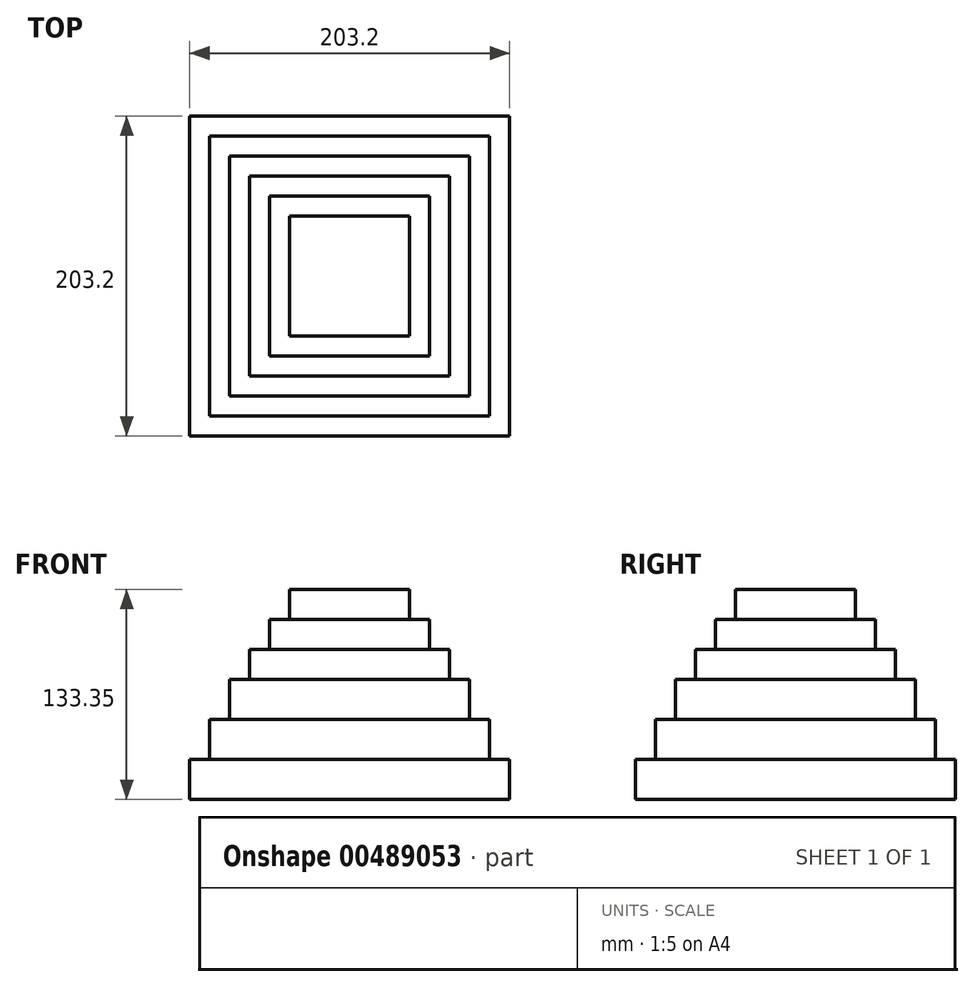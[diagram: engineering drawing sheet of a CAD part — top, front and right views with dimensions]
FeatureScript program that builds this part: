
annotation { "Feature Type Name" : "Feature", "Feature Type Description" : "" }
export const myFeature = defineFeature(function(context is Context, id is Id, definition is map)
    precondition{}
    {
        {
            var Q0;
            Q0=qCreatedBy(makeId("Top.planeOp"),FACE);
            var sketch = newSketch(context, id + "F0", { "sketchPlane" : qUnion([Q0])});
            skLineSegment(sketch, "E0.bottom", {"start": v(0, 0) * mm, "end": v(101.6, 0) * mm});
            skLineSegment(sketch, "E0.top", {"start": v(0, 101.6) * mm, "end": v(101.6, 101.6) * mm});
            skLineSegment(sketch, "E0.left", {"start": v(0, 0) * mm, "end": v(0, 101.6) * mm});
            skLineSegment(sketch, "E0.right", {"start": v(101.6, 0) * mm, "end": v(101.6, 101.6) * mm});
            skLineSegment(sketch, "E1.bottom", {"start": v(0, 0) * mm, "end": v(-101.6, 0) * mm});
            skLineSegment(sketch, "E1.top", {"start": v(0, -101.6) * mm, "end": v(-101.6, -101.6) * mm});
            skLineSegment(sketch, "E1.left", {"start": v(0, 0) * mm, "end": v(0, -101.6) * mm});
            skLineSegment(sketch, "E1.right", {"start": v(-101.6, 0) * mm, "end": v(-101.6, -101.6) * mm});
            skLineSegment(sketch, "E2.top", {"start": v(0, -101.6) * mm, "end": v(101.6, -101.6) * mm});
            skLineSegment(sketch, "E2.right", {"start": v(101.6, 0) * mm, "end": v(101.6, -101.6) * mm});
            skLineSegment(sketch, "E3.top", {"start": v(0, 101.6) * mm, "end": v(-101.6, 101.6) * mm});
            skLineSegment(sketch, "E3.right", {"start": v(-101.6, 0) * mm, "end": v(-101.6, 101.6) * mm});
            skSolve(sketch);
        }
        {
            var Q0;
            Q0 = qSketchRegion(id + "F0", true);
            extrude(context, id + "F1", {"entities" : qUnion([Q0]), "depth" : 25.4 * mm});
        }
        {
            var Q0;
            Q0=makeQuery(id+"F1.opExtrude","CAP_FACE",FACE,{"disambiguationData":[OSD([sQuery(id+"F0.wireOp",EDGE,"E0.top"),sQuery(id+"F0.wireOp",EDGE,"E0.right"),sQuery(id+"F0.wireOp",EDGE,"E1.top"),sQuery(id+"F0.wireOp",EDGE,"E1.right"),sQuery(id+"F0.wireOp",EDGE,"E2.top"),sQuery(id+"F0.wireOp",EDGE,"E2.right"),sQuery(id+"F0.wireOp",EDGE,"E3.top"),sQuery(id+"F0.wireOp",EDGE,"E3.right")])],"isStart":false});
            var sketch = newSketch(context, id + "F2", { "sketchPlane" : qUnion([Q0])});
            skLineSegment(sketch, "E4.bottom", {"start": v(0, 0) * mm, "end": v(-88.9, 0) * mm});
            skLineSegment(sketch, "E4.top", {"start": v(0, 88.9) * mm, "end": v(-88.9, 88.9) * mm});
            skLineSegment(sketch, "E4.left", {"start": v(0, 0) * mm, "end": v(0, 88.9) * mm});
            skLineSegment(sketch, "E4.right", {"start": v(-88.9, 0) * mm, "end": v(-88.9, 88.9) * mm});
            skLineSegment(sketch, "E5.bottom", {"start": v(0, 0) * mm, "end": v(88.9, 0) * mm});
            skLineSegment(sketch, "E5.top", {"start": v(0, 88.9) * mm, "end": v(88.9, 88.9) * mm});
            skLineSegment(sketch, "E5.right", {"start": v(88.9, 0) * mm, "end": v(88.9, 88.9) * mm});
            skLineSegment(sketch, "E6.top", {"start": v(0, -88.9) * mm, "end": v(88.9, -88.9) * mm});
            skLineSegment(sketch, "E6.left", {"start": v(0, 0) * mm, "end": v(0, -88.9) * mm});
            skLineSegment(sketch, "E6.right", {"start": v(88.9, 0) * mm, "end": v(88.9, -88.9) * mm});
            skLineSegment(sketch, "E7.top", {"start": v(0, -88.9) * mm, "end": v(-88.9, -88.9) * mm});
            skLineSegment(sketch, "E7.right", {"start": v(-88.9, 0) * mm, "end": v(-88.9, -88.9) * mm});
            skSolve(sketch);
        }
        {
            var Q0;
            Q0=makeQuery(id+"F2.imprint","IMPRINT",FACE,{"disambiguationData":[TD([[makeQuery(id+"F2.imprint","IMPRINT",EDGE,{"derivedFrom":sQuery(id+"F2.wireOp",EDGE,"E5.top")}),-1.0]])]});
            var Q1;
            Q1=makeQuery(id+"F2.imprint","IMPRINT",FACE,{"disambiguationData":[TD([[makeQuery(id+"F2.imprint","IMPRINT",EDGE,{"derivedFrom":sQuery(id+"F2.wireOp",EDGE,"E5.bottom")}),-1.0]])]});
            var Q2;
            Q2=makeQuery(id+"F2.imprint","IMPRINT",FACE,{"disambiguationData":[TD([[makeQuery(id+"F2.imprint","IMPRINT",EDGE,{"derivedFrom":sQuery(id+"F2.wireOp",EDGE,"E4.bottom")}),1.0]])]});
            var Q3;
            Q3=makeQuery(id+"F2.imprint","IMPRINT",FACE,{"disambiguationData":[TD([[makeQuery(id+"F2.imprint","IMPRINT",EDGE,{"derivedFrom":sQuery(id+"F2.wireOp",EDGE,"E4.top")}),1.0]])]});
            extrude(context, id + "F3", {"entities" : qUnion([Q0, Q1, Q2, Q3]), "operationType" : NewBodyOperationType.ADD, "depth" : 25.4 * mm});
        }
        {
            var Q0;
            Q0=makeQuery(id+"F3.opExtrude","CAP_FACE",FACE,{"disambiguationData":[OSD([sQuery(id+"F2.wireOp",EDGE,"E4.top"),sQuery(id+"F2.wireOp",EDGE,"E4.right"),sQuery(id+"F2.wireOp",EDGE,"E5.top"),sQuery(id+"F2.wireOp",EDGE,"E5.right"),sQuery(id+"F2.wireOp",EDGE,"E6.top"),sQuery(id+"F2.wireOp",EDGE,"E6.right"),sQuery(id+"F2.wireOp",EDGE,"E7.top"),sQuery(id+"F2.wireOp",EDGE,"E7.right")])],"isStart":false});
            var sketch = newSketch(context, id + "F4", { "sketchPlane" : qUnion([Q0])});
            skLineSegment(sketch, "E8.bottom", {"start": v(0, 0) * mm, "end": v(-76.2, 0) * mm});
            skLineSegment(sketch, "E8.top", {"start": v(0, 76.2) * mm, "end": v(-76.2, 76.2) * mm});
            skLineSegment(sketch, "E8.left", {"start": v(0, 0) * mm, "end": v(0, 76.2) * mm});
            skLineSegment(sketch, "E8.right", {"start": v(-76.2, 0) * mm, "end": v(-76.2, 76.2) * mm});
            skLineSegment(sketch, "E9.bottom", {"start": v(0, 0) * mm, "end": v(76.2, 0) * mm});
            skLineSegment(sketch, "E9.top", {"start": v(0, 76.2) * mm, "end": v(76.2, 76.2) * mm});
            skLineSegment(sketch, "E9.right", {"start": v(76.2, 0) * mm, "end": v(76.2, 76.2) * mm});
            skLineSegment(sketch, "E10.top", {"start": v(0, -76.2) * mm, "end": v(76.2, -76.2) * mm});
            skLineSegment(sketch, "E10.left", {"start": v(0, 0) * mm, "end": v(0, -76.2) * mm});
            skLineSegment(sketch, "E10.right", {"start": v(76.2, 0) * mm, "end": v(76.2, -76.2) * mm});
            skLineSegment(sketch, "E11.top", {"start": v(0, -76.2) * mm, "end": v(-76.2, -76.2) * mm});
            skLineSegment(sketch, "E11.right", {"start": v(-76.2, 0) * mm, "end": v(-76.2, -76.2) * mm});
            skSolve(sketch);
        }
        {
            var Q0;
            Q0=makeQuery(id+"F4.imprint","IMPRINT",FACE,{"disambiguationData":[TD([[makeQuery(id+"F4.imprint","IMPRINT",EDGE,{"derivedFrom":sQuery(id+"F4.wireOp",EDGE,"E9.top")}),-1.0]])]});
            var Q1;
            Q1=makeQuery(id+"F4.imprint","IMPRINT",FACE,{"disambiguationData":[TD([[makeQuery(id+"F4.imprint","IMPRINT",EDGE,{"derivedFrom":sQuery(id+"F4.wireOp",EDGE,"E9.bottom")}),-1.0]])]});
            var Q2;
            Q2=makeQuery(id+"F4.imprint","IMPRINT",FACE,{"disambiguationData":[TD([[makeQuery(id+"F4.imprint","IMPRINT",EDGE,{"derivedFrom":sQuery(id+"F4.wireOp",EDGE,"E8.bottom")}),1.0]])]});
            var Q3;
            Q3=makeQuery(id+"F4.imprint","IMPRINT",FACE,{"disambiguationData":[TD([[makeQuery(id+"F4.imprint","IMPRINT",EDGE,{"derivedFrom":sQuery(id+"F4.wireOp",EDGE,"E8.top")}),1.0]])]});
            extrude(context, id + "F5", {"entities" : qUnion([Q0, Q1, Q2, Q3]), "operationType" : NewBodyOperationType.ADD, "depth" : 25.4 * mm});
        }
        {
            var Q0;
            Q0=makeQuery(id+"F5.opExtrude","CAP_FACE",FACE,{"disambiguationData":[OSD([sQuery(id+"F4.wireOp",EDGE,"E8.top"),sQuery(id+"F4.wireOp",EDGE,"E8.right"),sQuery(id+"F4.wireOp",EDGE,"E9.top"),sQuery(id+"F4.wireOp",EDGE,"E9.right"),sQuery(id+"F4.wireOp",EDGE,"E10.top"),sQuery(id+"F4.wireOp",EDGE,"E10.right"),sQuery(id+"F4.wireOp",EDGE,"E11.top"),sQuery(id+"F4.wireOp",EDGE,"E11.right")])],"isStart":false});
            var sketch = newSketch(context, id + "F6", { "sketchPlane" : qUnion([Q0])});
            skLineSegment(sketch, "E12.bottom", {"start": v(0, 0) * mm, "end": v(-63.5, 0) * mm});
            skLineSegment(sketch, "E12.top", {"start": v(0, 63.5) * mm, "end": v(-63.5, 63.5) * mm});
            skLineSegment(sketch, "E12.left", {"start": v(0, 0) * mm, "end": v(0, 63.5) * mm});
            skLineSegment(sketch, "E12.right", {"start": v(-63.5, 0) * mm, "end": v(-63.5, 63.5) * mm});
            skLineSegment(sketch, "E13.bottom", {"start": v(0, 0) * mm, "end": v(63.5, 0) * mm});
            skLineSegment(sketch, "E13.top", {"start": v(0, -63.5) * mm, "end": v(63.5, -63.5) * mm});
            skLineSegment(sketch, "E13.left", {"start": v(0, 0) * mm, "end": v(0, -63.5) * mm});
            skLineSegment(sketch, "E13.right", {"start": v(63.5, 0) * mm, "end": v(63.5, -63.5) * mm});
            skLineSegment(sketch, "E14.top", {"start": v(0, -63.5) * mm, "end": v(-63.5, -63.5) * mm});
            skLineSegment(sketch, "E14.right", {"start": v(-63.5, 0) * mm, "end": v(-63.5, -63.5) * mm});
            skLineSegment(sketch, "E15.top", {"start": v(0, 63.5) * mm, "end": v(63.5, 63.5) * mm});
            skLineSegment(sketch, "E15.right", {"start": v(63.5, 0) * mm, "end": v(63.5, 63.5) * mm});
            skSolve(sketch);
        }
        {
            var Q0;
            Q0=makeQuery(id+"F6.imprint","IMPRINT",FACE,{"disambiguationData":[TD([[makeQuery(id+"F6.imprint","IMPRINT",EDGE,{"derivedFrom":sQuery(id+"F6.wireOp",EDGE,"E13.top")}),1.0]])]});
            var Q1;
            Q1=makeQuery(id+"F6.imprint","IMPRINT",FACE,{"disambiguationData":[TD([[makeQuery(id+"F6.imprint","IMPRINT",EDGE,{"derivedFrom":sQuery(id+"F6.wireOp",EDGE,"E12.bottom")}),1.0]])]});
            var Q2;
            Q2=makeQuery(id+"F6.imprint","IMPRINT",FACE,{"disambiguationData":[TD([[makeQuery(id+"F6.imprint","IMPRINT",EDGE,{"derivedFrom":sQuery(id+"F6.wireOp",EDGE,"E13.bottom")}),1.0]])]});
            var Q3;
            Q3=makeQuery(id+"F6.imprint","IMPRINT",FACE,{"disambiguationData":[TD([[makeQuery(id+"F6.imprint","IMPRINT",EDGE,{"derivedFrom":sQuery(id+"F6.wireOp",EDGE,"E12.top")}),1.0]])]});
            extrude(context, id + "F7", {"entities" : qUnion([Q0, Q1, Q2, Q3]), "operationType" : NewBodyOperationType.ADD, "depth" : 19.05 * mm});
        }
        {
            var Q0;
            Q0=makeQuery(id+"F7.opExtrude","CAP_FACE",FACE,{"disambiguationData":[OSD([sQuery(id+"F6.wireOp",EDGE,"E12.top"),sQuery(id+"F6.wireOp",EDGE,"E12.right"),sQuery(id+"F6.wireOp",EDGE,"E13.top"),sQuery(id+"F6.wireOp",EDGE,"E13.right"),sQuery(id+"F6.wireOp",EDGE,"E14.top"),sQuery(id+"F6.wireOp",EDGE,"E14.right"),sQuery(id+"F6.wireOp",EDGE,"E15.top"),sQuery(id+"F6.wireOp",EDGE,"E15.right")])],"isStart":false});
            var sketch = newSketch(context, id + "F8", { "sketchPlane" : qUnion([Q0])});
            skLineSegment(sketch, "E16.bottom", {"start": v(0, 0) * mm, "end": v(50.8, 0) * mm});
            skLineSegment(sketch, "E16.top", {"start": v(0, 50.8) * mm, "end": v(50.8, 50.8) * mm});
            skLineSegment(sketch, "E16.left", {"start": v(0, 0) * mm, "end": v(0, 50.8) * mm});
            skLineSegment(sketch, "E16.right", {"start": v(50.8, 0) * mm, "end": v(50.8, 50.8) * mm});
            skLineSegment(sketch, "E17.top", {"start": v(0, -50.8) * mm, "end": v(50.8, -50.8) * mm});
            skLineSegment(sketch, "E17.left", {"start": v(0, 0) * mm, "end": v(0, -50.8) * mm});
            skLineSegment(sketch, "E17.right", {"start": v(50.8, 0) * mm, "end": v(50.8, -50.8) * mm});
            skLineSegment(sketch, "E18.bottom", {"start": v(0, 0) * mm, "end": v(-50.8, 0) * mm});
            skLineSegment(sketch, "E18.top", {"start": v(0, -50.8) * mm, "end": v(-50.8, -50.8) * mm});
            skLineSegment(sketch, "E18.right", {"start": v(-50.8, 0) * mm, "end": v(-50.8, -50.8) * mm});
            skLineSegment(sketch, "E19.top", {"start": v(0, 50.8) * mm, "end": v(-50.8, 50.8) * mm});
            skLineSegment(sketch, "E19.right", {"start": v(-50.8, 0) * mm, "end": v(-50.8, 50.8) * mm});
            skSolve(sketch);
        }
        {
            var Q0;
            Q0=makeQuery(id+"F8.imprint","IMPRINT",FACE,{"disambiguationData":[TD([[makeQuery(id+"F8.imprint","IMPRINT",EDGE,{"derivedFrom":sQuery(id+"F8.wireOp",EDGE,"E16.top")}),-1.0]])]});
            var Q1;
            Q1=makeQuery(id+"F8.imprint","IMPRINT",FACE,{"disambiguationData":[TD([[makeQuery(id+"F8.imprint","IMPRINT",EDGE,{"derivedFrom":sQuery(id+"F8.wireOp",EDGE,"E16.bottom")}),-1.0]])]});
            var Q2;
            Q2=makeQuery(id+"F8.imprint","IMPRINT",FACE,{"disambiguationData":[TD([[makeQuery(id+"F8.imprint","IMPRINT",EDGE,{"derivedFrom":sQuery(id+"F8.wireOp",EDGE,"E18.top")}),-1.0]])]});
            var Q3;
            Q3=makeQuery(id+"F8.imprint","IMPRINT",FACE,{"disambiguationData":[TD([[makeQuery(id+"F8.imprint","IMPRINT",EDGE,{"derivedFrom":sQuery(id+"F8.wireOp",EDGE,"E18.bottom")}),-1.0]])]});
            extrude(context, id + "F9", {"entities" : qUnion([Q0, Q1, Q2, Q3]), "operationType" : NewBodyOperationType.ADD, "depth" : 19.05 * mm});
        }
        {
            var Q0;
            Q0=makeQuery(id+"F9.opExtrude","CAP_FACE",FACE,{"disambiguationData":[OSD([sQuery(id+"F8.wireOp",EDGE,"E16.top"),sQuery(id+"F8.wireOp",EDGE,"E16.right"),sQuery(id+"F8.wireOp",EDGE,"E17.top"),sQuery(id+"F8.wireOp",EDGE,"E17.right"),sQuery(id+"F8.wireOp",EDGE,"E18.top"),sQuery(id+"F8.wireOp",EDGE,"E18.right"),sQuery(id+"F8.wireOp",EDGE,"E19.top"),sQuery(id+"F8.wireOp",EDGE,"E19.right")])],"isStart":false});
            var sketch = newSketch(context, id + "F10", { "sketchPlane" : qUnion([Q0])});
            skLineSegment(sketch, "E20.bottom", {"start": v(0, 0) * mm, "end": v(-38.1, 0) * mm});
            skLineSegment(sketch, "E20.top", {"start": v(0, -38.1) * mm, "end": v(-38.1, -38.1) * mm});
            skLineSegment(sketch, "E20.left", {"start": v(0, 0) * mm, "end": v(0, -38.1) * mm});
            skLineSegment(sketch, "E20.right", {"start": v(-38.1, 0) * mm, "end": v(-38.1, -38.1) * mm});
            skLineSegment(sketch, "E21.bottom", {"start": v(0, 0) * mm, "end": v(38.1, 0) * mm});
            skLineSegment(sketch, "E21.top", {"start": v(0, 38.1) * mm, "end": v(38.1, 38.1) * mm});
            skLineSegment(sketch, "E21.left", {"start": v(0, 0) * mm, "end": v(0, 38.1) * mm});
            skLineSegment(sketch, "E21.right", {"start": v(38.1, 0) * mm, "end": v(38.1, 38.1) * mm});
            skLineSegment(sketch, "E22.top", {"start": v(0, -38.1) * mm, "end": v(38.1, -38.1) * mm});
            skLineSegment(sketch, "E22.right", {"start": v(38.1, 0) * mm, "end": v(38.1, -38.1) * mm});
            skLineSegment(sketch, "E23.top", {"start": v(0, 38.1) * mm, "end": v(-38.1, 38.1) * mm});
            skLineSegment(sketch, "E23.right", {"start": v(-38.1, 0) * mm, "end": v(-38.1, 38.1) * mm});
            skSolve(sketch);
        }
        {
            var Q0;
            Q0 = qSketchRegion(id + "F10", true);
            extrude(context, id + "F11", {"entities" : qUnion([Q0]), "operationType" : NewBodyOperationType.ADD, "depth" : 19.05 * mm});
        }
    });
